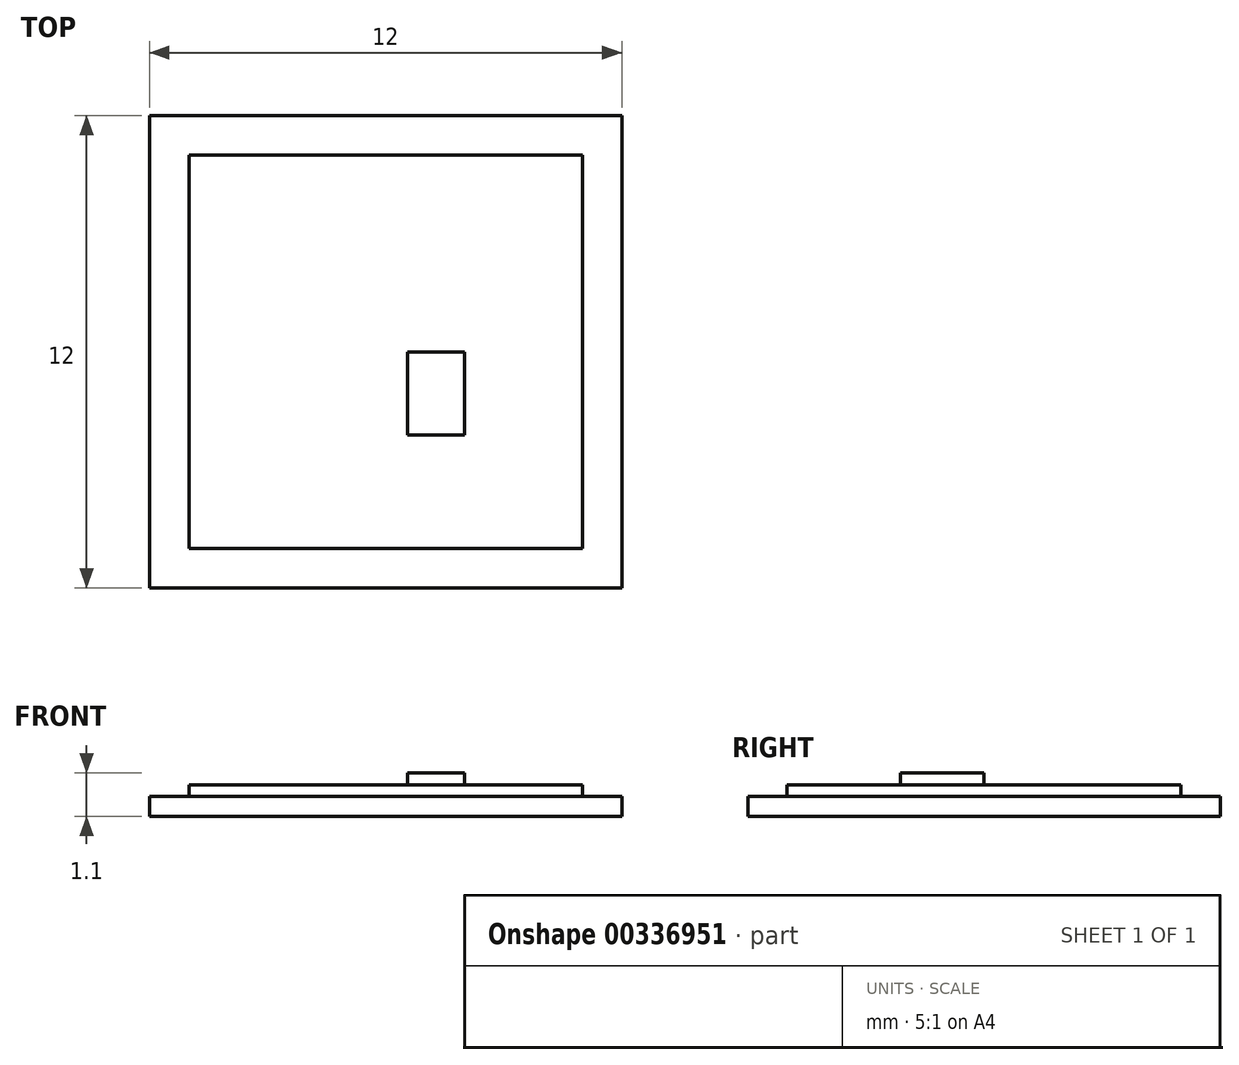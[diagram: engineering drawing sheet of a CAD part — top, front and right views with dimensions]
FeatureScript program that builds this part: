
annotation { "Feature Type Name" : "Feature", "Feature Type Description" : "" }
export const myFeature = defineFeature(function(context is Context, id is Id, definition is map)
    precondition{}
    {
        {
            var Q0;
            Q0=qCreatedBy(makeId("Front.planeOp"),FACE);
            var sketch = newSketch(context, id + "F0", { "sketchPlane" : qUnion([Q0])});
            skLineSegment(sketch, "E0.bottom", {"start": v(-5, -0.3) * mm, "end": v(5, -0.3) * mm});
            skLineSegment(sketch, "E0.top", {"start": v(-5, 0) * mm, "end": v(5, 0) * mm});
            skLineSegment(sketch, "E0.left", {"start": v(-5, -0.3) * mm, "end": v(-5, 0) * mm});
            skLineSegment(sketch, "E0.right", {"start": v(5, -0.3) * mm, "end": v(5, 0) * mm});
            skSolve(sketch);
        }
        {
            var Q0;
            Q0=makeQuery(id+"F0.imprint","IMPRINT",FACE,{"disambiguationData":[TD([[makeQuery(id+"F0.imprint","IMPRINT",EDGE,{"derivedFrom":sQuery(id+"F0.wireOp",EDGE,"E0.bottom")}),1.0]])]});
            extrude(context, id + "F1", {"entities" : qUnion([Q0]), "endBound" : BoundingType.SYMMETRIC, "depth" : 10 * mm});
        }
        {
            var Q0;
            Q0=qCreatedBy(makeId("Front.planeOp"),FACE);
            var sketch = newSketch(context, id + "F2", { "sketchPlane" : qUnion([Q0])});
            skLineSegment(sketch, "E1.bottom", {"start": v(0.56, 0.3) * mm, "end": v(2, 0.3) * mm});
            skLineSegment(sketch, "E1.top", {"start": v(0.56, 0) * mm, "end": v(2, 0) * mm});
            skLineSegment(sketch, "E1.left", {"start": v(0.56, 0.3) * mm, "end": v(0.56, 0) * mm});
            skLineSegment(sketch, "E1.right", {"start": v(2, 0.3) * mm, "end": v(2, 0) * mm});
            skSolve(sketch);
        }
        {
            var Q0;
            Q0=makeQuery(id+"F2.imprint","IMPRINT",FACE,{"disambiguationData":[TD([[makeQuery(id+"F2.imprint","IMPRINT",EDGE,{"derivedFrom":sQuery(id+"F2.wireOp",EDGE,"E1.bottom")}),-1.0]])]});
            extrude(context, id + "F3", {"entities" : qUnion([Q0]), "depth" : 2.12 * mm});
        }
        {
            var Q0;
            Q0=qCreatedBy(makeId("Front.planeOp"),FACE);
            var sketch = newSketch(context, id + "F4", { "sketchPlane" : qUnion([Q0])});
            skLineSegment(sketch, "E2.bottom", {"start": v(-6, -0.3) * mm, "end": v(6, -0.3) * mm});
            skLineSegment(sketch, "E2.top", {"start": v(-6, -0.8) * mm, "end": v(6, -0.8) * mm});
            skLineSegment(sketch, "E2.left", {"start": v(-6, -0.3) * mm, "end": v(-6, -0.8) * mm});
            skLineSegment(sketch, "E2.right", {"start": v(6, -0.3) * mm, "end": v(6, -0.8) * mm});
            skSolve(sketch);
        }
        {
            var Q0;
            Q0=makeQuery(id+"F4.imprint","IMPRINT",FACE,{"disambiguationData":[TD([[makeQuery(id+"F4.imprint","IMPRINT",EDGE,{"derivedFrom":sQuery(id+"F4.wireOp",EDGE,"E2.bottom")}),-1.0]])]});
            extrude(context, id + "F5", {"entities" : qUnion([Q0]), "endBound" : BoundingType.SYMMETRIC, "depth" : 12 * mm});
        }
    });
